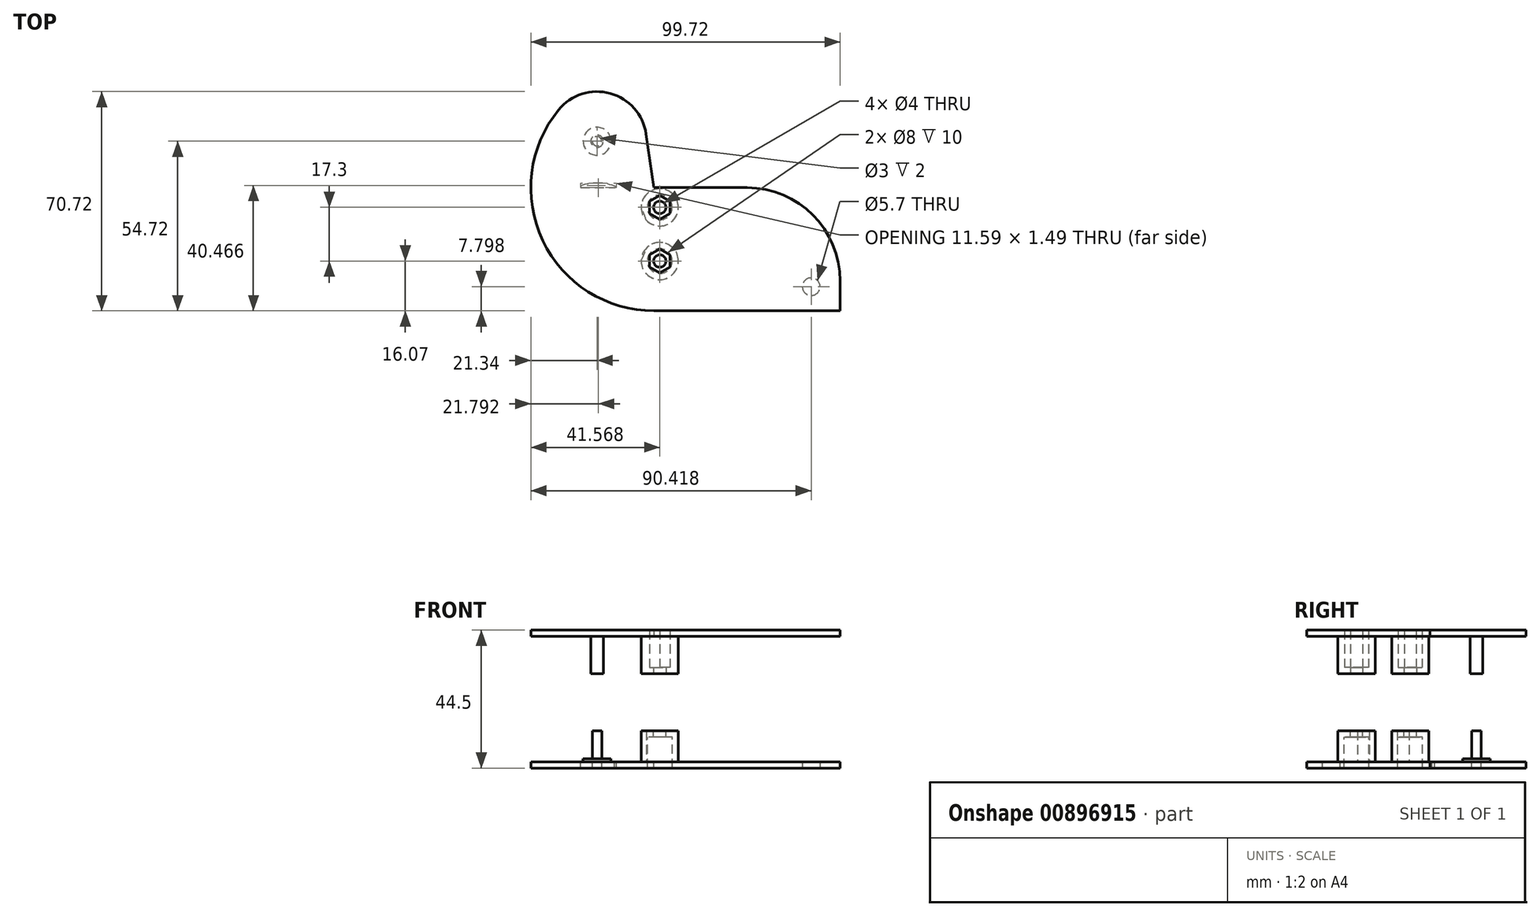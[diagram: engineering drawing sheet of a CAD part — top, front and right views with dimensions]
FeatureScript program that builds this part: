
annotation { "Feature Type Name" : "Feature", "Feature Type Description" : "" }
export const myFeature = defineFeature(function(context is Context, id is Id, definition is map)
    precondition{}
    {
        {
            var Q0;
            Q0=qCreatedBy(makeId("Top.planeOp"),FACE);
            var sketch = newSketch(context, id + "F0", { "sketchPlane" : qUnion([Q0])});
            skPoint(sketch, "E0", {"position": v(20.23, 8.65) * mm});
            skPoint(sketch, "E1", {"position": v(20.23, -8.65) * mm});
            skPoint(sketch, "E2", {"position": v(0, 0) * mm});
            skPoint(sketch, "E3", {"position": v(0, 30) * mm});
            skCircle(sketch, "E4", {"center": v(18.38, 15) * mm, "radius": 23.72 * mm});
            skCircle(sketch, "E5.0", {"center": v(18.38, 15) * mm, "radius": 39.72 * mm});
            skCircle(sketch, "E6", {"center": v(0, 0) * mm, "radius": 16.5 * mm});
            skCircle(sketch, "E7", {"center": v(0, 30) * mm, "radius": 19 * mm});
            skLineSegment(sketch, "E8", {"start": v(-21.34, 15) * mm, "end": v(18.38, 15) * mm});
            skLineSegment(sketch, "E9", {"start": v(18.38, 15) * mm, "end": v(58.1, 15) * mm});
            skLineSegment(sketch, "E10", {"start": v(18.38, -24.72) * mm, "end": v(78.38, -24.72) * mm});
            skLineSegment(sketch, "E11", {"start": v(78.38, -24.72) * mm, "end": v(78.38, 15) * mm});
            skLineSegment(sketch, "E12", {"start": v(78.38, 15) * mm, "end": v(58.1, 15) * mm});
            skCircle(sketch, "E13", {"center": v(20.23, -8.65) * mm, "radius": 4 * mm});
            skCircle(sketch, "E14", {"center": v(20.23, 8.65) * mm, "radius": 4 * mm});
            skCircle(sketch, "E15.0", {"center": v(20.23, -8.65) * mm, "radius": 6 * mm});
            skCircle(sketch, "E16", {"center": v(20.23, 8.65) * mm, "radius": 6 * mm});
            skLineSegment(sketch, "E17", {"start": v(18.38, 15) * mm, "end": v(12.6, 54.3) * mm});
            skCircle(sketch, "E18", {"center": v(0, 30) * mm, "radius": 16 * mm});
            skCircle(sketch, "E19", {"center": v(0, 30) * mm, "radius": 1.5 * mm});
            skCircle(sketch, "E20.0", {"center": v(0, 30) * mm, "radius": 4.5 * mm});
            skSolve(sketch);
        }
        {
            var Q0;
            {var subQ2=sQuery(id+"F0.wireOp",EDGE,"E10");Q0=makeQuery(id+"F0.imprint","IMPRINT",FACE,{"disambiguationData":[TD([[makeQuery(id+"F0.imprint","IMPRINT",EDGE,{"derivedFrom":subQ2}),1.0]])]});}
            var Q1;
            {var subQ4=sQuery(id+"F0.wireOp",EDGE,"E6");var subQ5=sQuery(id+"F0.wireOp",EDGE,"E4");var subQ6=makeQuery(id+"F0.imprint","INTERSECT",VERTEX,{"disambiguationData":[OD(1.0)],"derivedFrom":[subQ5,subQ4]});Q1=makeQuery(id+"F0.imprint","IMPRINT",FACE,{"disambiguationData":[TD([[makeQuery(id+"F0.imprint","IMPRINT",EDGE,{"disambiguationData":[TD([[subQ6,-1.0]])],"derivedFrom":subQ5}),-1.0]])]});}
            var Q2;
            {var subQ0=sQuery(id+"F0.wireOp",EDGE,"E15.0");var subQ1=sQuery(id+"F0.wireOp",EDGE,"E4");var subQ2=makeQuery(id+"F0.imprint","INTERSECT",VERTEX,{"disambiguationData":[OD(0.0)],"derivedFrom":[subQ1,subQ0]});Q2=makeQuery(id+"F0.imprint","IMPRINT",FACE,{"disambiguationData":[TD([[makeQuery(id+"F0.imprint","IMPRINT",EDGE,{"disambiguationData":[TD([[subQ2,-1.0]])],"derivedFrom":subQ1}),-1.0]])]});}
            var Q3;
            {var subQ0=sQuery(id+"F0.wireOp",EDGE,"E15.0");var subQ1=sQuery(id+"F0.wireOp",EDGE,"E4");var subQ2=makeQuery(id+"F0.imprint","INTERSECT",VERTEX,{"disambiguationData":[OD(0.0)],"derivedFrom":[subQ1,subQ0]});Q3=makeQuery(id+"F0.imprint","IMPRINT",FACE,{"disambiguationData":[TD([[makeQuery(id+"F0.imprint","IMPRINT",EDGE,{"disambiguationData":[TD([[subQ2,-1.0]])],"derivedFrom":subQ1}),1.0]])]});}
            var Q4;
            Q4=makeQuery(id+"F0.imprint","IMPRINT",FACE,{"disambiguationData":[TD([[makeQuery(id+"F0.imprint","IMPRINT",EDGE,{"derivedFrom":sQuery(id+"F0.wireOp",EDGE,"E14")}),-1.0]])]});
            var Q5;
            Q5=makeQuery(id+"F0.imprint","IMPRINT",FACE,{"disambiguationData":[TD([[makeQuery(id+"F0.imprint","IMPRINT",EDGE,{"derivedFrom":sQuery(id+"F0.wireOp",EDGE,"E16")}),-1.0]])]});
            var Q6;
            {var subQ0=sQuery(id+"F0.wireOp",EDGE,"E7");var subQ1=sQuery(id+"F0.wireOp",EDGE,"E4");var subQ2=makeQuery(id+"F0.imprint","INTERSECT",VERTEX,{"disambiguationData":[OD(1.0)],"derivedFrom":[subQ1,subQ0]});Q6=makeQuery(id+"F0.imprint","IMPRINT",FACE,{"disambiguationData":[TD([[makeQuery(id+"F0.imprint","IMPRINT",EDGE,{"disambiguationData":[TD([[subQ2,-1.0]])],"derivedFrom":subQ1}),1.0]])]});}
            var Q7;
            {var subQ0=sQuery(id+"F0.wireOp",EDGE,"E8");var subQ1=sQuery(id+"F0.wireOp",EDGE,"E4");var subQ2=makeQuery(id+"F0.imprint","INTERSECT",VERTEX,{"derivedFrom":[subQ1,subQ0]});Q7=makeQuery(id+"F0.imprint","IMPRINT",FACE,{"disambiguationData":[TD([[makeQuery(id+"F0.imprint","IMPRINT",EDGE,{"disambiguationData":[TD([[subQ2,-1.0]])],"derivedFrom":subQ1}),1.0]])]});}
            var Q8;
            {var subQ3=sQuery(id+"F0.wireOp",EDGE,"E4");var subQ6=sQuery(id+"F0.wireOp",EDGE,"E7");var subQ8=makeQuery(id+"F0.imprint","INTERSECT",VERTEX,{"disambiguationData":[OD(1.0)],"derivedFrom":[subQ3,subQ6]});Q8=makeQuery(id+"F0.imprint","IMPRINT",FACE,{"disambiguationData":[TD([[makeQuery(id+"F0.imprint","IMPRINT",EDGE,{"disambiguationData":[TD([[subQ8,-1.0]])],"derivedFrom":subQ3}),-1.0]])]});}
            var Q9;
            {var subQ0=sQuery(id+"F0.wireOp",EDGE,"E8");var subQ1=sQuery(id+"F0.wireOp",EDGE,"E4");var subQ2=makeQuery(id+"F0.imprint","INTERSECT",VERTEX,{"derivedFrom":[subQ1,subQ0]});Q9=makeQuery(id+"F0.imprint","IMPRINT",FACE,{"disambiguationData":[TD([[makeQuery(id+"F0.imprint","IMPRINT",EDGE,{"disambiguationData":[TD([[subQ2,-1.0]])],"derivedFrom":subQ1}),-1.0]])]});}
            var Q10;
            {var subQ0=sQuery(id+"F0.wireOp",EDGE,"E8");var subQ1=sQuery(id+"F0.wireOp",EDGE,"E5.0");var subQ2=makeQuery(id+"F0.imprint","INTERSECT",VERTEX,{"derivedFrom":[subQ1,subQ0]});Q10=makeQuery(id+"F0.imprint","IMPRINT",FACE,{"disambiguationData":[TD([[makeQuery(id+"F0.imprint","IMPRINT",EDGE,{"disambiguationData":[TD([[subQ2,-1.0]])],"derivedFrom":subQ1}),1.0]])]});}
            var Q11;
            {var subQ0=sQuery(id+"F0.wireOp",EDGE,"E8");var subQ1=sQuery(id+"F0.wireOp",EDGE,"E5.0");var subQ2=makeQuery(id+"F0.imprint","INTERSECT",VERTEX,{"derivedFrom":[subQ1,subQ0]});Q11=makeQuery(id+"F0.imprint","IMPRINT",FACE,{"disambiguationData":[TD([[makeQuery(id+"F0.imprint","IMPRINT",EDGE,{"disambiguationData":[TD([[subQ2,1.0]])],"derivedFrom":subQ1}),1.0]])]});}
            var Q12;
            {var subQ0=sQuery(id+"F0.wireOp",EDGE,"E6");var subQ1=sQuery(id+"F0.wireOp",EDGE,"E4");var subQ2=makeQuery(id+"F0.imprint","INTERSECT",VERTEX,{"disambiguationData":[OD(0.0)],"derivedFrom":[subQ1,subQ0]});Q12=makeQuery(id+"F0.imprint","IMPRINT",FACE,{"disambiguationData":[TD([[makeQuery(id+"F0.imprint","IMPRINT",EDGE,{"disambiguationData":[TD([[subQ2,-1.0]])],"derivedFrom":subQ1}),1.0]])]});}
            var Q13;
            {var subQ0=sQuery(id+"F0.wireOp",EDGE,"E6");var subQ1=sQuery(id+"F0.wireOp",EDGE,"E4");var subQ2=makeQuery(id+"F0.imprint","INTERSECT",VERTEX,{"disambiguationData":[OD(0.0)],"derivedFrom":[subQ1,subQ0]});Q13=makeQuery(id+"F0.imprint","IMPRINT",FACE,{"disambiguationData":[TD([[makeQuery(id+"F0.imprint","IMPRINT",EDGE,{"disambiguationData":[TD([[subQ2,-1.0]])],"derivedFrom":subQ1}),-1.0]])]});}
            var Q14;
            {var subQ0=sQuery(id+"F0.wireOp",EDGE,"E17");var subQ1=sQuery(id+"F0.wireOp",EDGE,"E7");var subQ2=makeQuery(id+"F0.imprint","INTERSECT",VERTEX,{"derivedFrom":[subQ1,subQ0]});Q14=makeQuery(id+"F0.imprint","IMPRINT",FACE,{"disambiguationData":[TD([[makeQuery(id+"F0.imprint","IMPRINT",EDGE,{"disambiguationData":[TD([[subQ2,1.0]])],"derivedFrom":subQ1}),-1.0]])]});}
            var Q15;
            {var subQ0=sQuery(id+"F0.wireOp",EDGE,"E18");var subQ1=sQuery(id+"F0.wireOp",EDGE,"E4");var subQ2=makeQuery(id+"F0.imprint","INTERSECT",VERTEX,{"disambiguationData":[OD(0.0)],"derivedFrom":[subQ1,subQ0]});Q15=makeQuery(id+"F0.imprint","IMPRINT",FACE,{"disambiguationData":[TD([[makeQuery(id+"F0.imprint","IMPRINT",EDGE,{"disambiguationData":[TD([[subQ2,-1.0]])],"derivedFrom":subQ1}),-1.0]])]});}
            var Q16;
            {var subQ5=sQuery(id+"F0.wireOp",EDGE,"E4");var subQ7=sQuery(id+"F0.wireOp",EDGE,"E18");var subQ8=makeQuery(id+"F0.imprint","INTERSECT",VERTEX,{"disambiguationData":[OD(1.0)],"derivedFrom":[subQ5,subQ7]});Q16=makeQuery(id+"F0.imprint","IMPRINT",FACE,{"disambiguationData":[TD([[makeQuery(id+"F0.imprint","IMPRINT",EDGE,{"disambiguationData":[TD([[subQ8,-1.0]])],"derivedFrom":subQ5}),-1.0]])]});}
            var Q17;
            {var subQ0=sQuery(id+"F0.wireOp",EDGE,"63ee93db-11cd-4e26-b8ef-de9a7e97acbf.0");var subQ1=sQuery(id+"F0.wireOp",EDGE,"E4");var subQ2=makeQuery(id+"F0.imprint","INTERSECT",VERTEX,{"disambiguationData":[OD(0.0)],"derivedFrom":[subQ1,subQ0]});Q17=makeQuery(id+"F0.imprint","IMPRINT",FACE,{"disambiguationData":[TD([[makeQuery(id+"F0.imprint","IMPRINT",EDGE,{"disambiguationData":[TD([[subQ2,-1.0]])],"derivedFrom":subQ1}),1.0]])]});}
            var Q18;
            {var subQ0=sQuery(id+"F0.wireOp",EDGE,"63ee93db-11cd-4e26-b8ef-de9a7e97acbf.0");var subQ1=sQuery(id+"F0.wireOp",EDGE,"E4");var subQ2=makeQuery(id+"F0.imprint","INTERSECT",VERTEX,{"disambiguationData":[OD(0.0)],"derivedFrom":[subQ1,subQ0]});Q18=makeQuery(id+"F0.imprint","IMPRINT",FACE,{"disambiguationData":[TD([[makeQuery(id+"F0.imprint","IMPRINT",EDGE,{"disambiguationData":[TD([[subQ2,-1.0]])],"derivedFrom":subQ1}),-1.0]])]});}
            var Q19;
            {var subQ0=sQuery(id+"F0.wireOp",EDGE,"E20.0");var subQ1=sQuery(id+"F0.wireOp",EDGE,"E4");var subQ2=makeQuery(id+"F0.imprint","INTERSECT",VERTEX,{"disambiguationData":[OD(0.0)],"derivedFrom":[subQ1,subQ0]});Q19=makeQuery(id+"F0.imprint","IMPRINT",FACE,{"disambiguationData":[TD([[makeQuery(id+"F0.imprint","IMPRINT",EDGE,{"disambiguationData":[TD([[subQ2,-1.0]])],"derivedFrom":subQ1}),-1.0]])]});}
            var Q20;
            {var subQ0=sQuery(id+"F0.wireOp",EDGE,"E20.0");var subQ1=sQuery(id+"F0.wireOp",EDGE,"E4");var subQ2=makeQuery(id+"F0.imprint","INTERSECT",VERTEX,{"disambiguationData":[OD(0.0)],"derivedFrom":[subQ1,subQ0]});Q20=makeQuery(id+"F0.imprint","IMPRINT",FACE,{"disambiguationData":[TD([[makeQuery(id+"F0.imprint","IMPRINT",EDGE,{"disambiguationData":[TD([[subQ2,-1.0]])],"derivedFrom":subQ1}),1.0]])]});}
            var Q21;
            {var subQ3=sQuery(id+"F0.wireOp",EDGE,"E7");var subQ5=sQuery(id+"F0.wireOp",EDGE,"E5.0");var subQ6=makeQuery(id+"F0.imprint","INTERSECT",VERTEX,{"disambiguationData":[OD(1.0)],"derivedFrom":[subQ5,subQ3]});Q21=makeQuery(id+"F0.imprint","IMPRINT",FACE,{"disambiguationData":[TD([[makeQuery(id+"F0.imprint","IMPRINT",EDGE,{"disambiguationData":[TD([[subQ6,1.0]])],"derivedFrom":subQ5}),1.0]])]});}
            var Q22;
            {var subQ0=sQuery(id+"F0.wireOp",EDGE,"E8");var subQ1=sQuery(id+"F0.wireOp",EDGE,"E6");var subQ2=makeQuery(id+"F0.imprint","INTERSECT",VERTEX,{"disambiguationData":[OD(1.0)],"derivedFrom":[subQ1,subQ0]});Q22=makeQuery(id+"F0.imprint","IMPRINT",FACE,{"disambiguationData":[TD([[makeQuery(id+"F0.imprint","IMPRINT",EDGE,{"disambiguationData":[TD([[subQ2,-1.0]])],"derivedFrom":subQ1}),-1.0]])]});}
            var Q23;
            {var subQ0=sQuery(id+"F0.wireOp",EDGE,"E18");var subQ1=sQuery(id+"F0.wireOp",EDGE,"E6");var subQ2=makeQuery(id+"F0.imprint","INTERSECT",VERTEX,{"disambiguationData":[OD(1.0)],"derivedFrom":[subQ1,subQ0]});Q23=makeQuery(id+"F0.imprint","IMPRINT",FACE,{"disambiguationData":[TD([[makeQuery(id+"F0.imprint","IMPRINT",EDGE,{"disambiguationData":[TD([[subQ2,-1.0]])],"derivedFrom":subQ1}),1.0]])]});}
            var Q24;
            {var subQ5=sQuery(id+"F0.wireOp",EDGE,"E8");var subQ7=sQuery(id+"F0.wireOp",EDGE,"E6");var subQ9=makeQuery(id+"F0.imprint","INTERSECT",VERTEX,{"disambiguationData":[OD(0.0)],"derivedFrom":[subQ7,subQ5]});Q24=makeQuery(id+"F0.imprint","IMPRINT",FACE,{"disambiguationData":[TD([[makeQuery(id+"F0.imprint","IMPRINT",EDGE,{"disambiguationData":[TD([[subQ9,-1.0]])],"derivedFrom":subQ7}),-1.0]])]});}
            var Q25;
            {var subQ0=sQuery(id+"F0.wireOp",EDGE,"E8");var subQ1=sQuery(id+"F0.wireOp",EDGE,"E6");var subQ2=makeQuery(id+"F0.imprint","INTERSECT",VERTEX,{"disambiguationData":[OD(0.0)],"derivedFrom":[subQ1,subQ0]});Q25=makeQuery(id+"F0.imprint","IMPRINT",FACE,{"disambiguationData":[TD([[makeQuery(id+"F0.imprint","IMPRINT",EDGE,{"disambiguationData":[TD([[subQ2,1.0]])],"derivedFrom":subQ1}),-1.0]])]});}
            var Q26;
            {var subQ0=sQuery(id+"F0.wireOp",EDGE,"E18");var subQ1=sQuery(id+"F0.wireOp",EDGE,"E4");var subQ2=makeQuery(id+"F0.imprint","INTERSECT",VERTEX,{"disambiguationData":[OD(0.0)],"derivedFrom":[subQ1,subQ0]});Q26=makeQuery(id+"F0.imprint","IMPRINT",FACE,{"disambiguationData":[TD([[makeQuery(id+"F0.imprint","IMPRINT",EDGE,{"disambiguationData":[TD([[subQ2,-1.0]])],"derivedFrom":subQ1}),1.0]])]});}
            var Q27;
            {var subQ0=sQuery(id+"F0.wireOp",EDGE,"E8");var subQ1=sQuery(id+"F0.wireOp",EDGE,"E6");var subQ2=makeQuery(id+"F0.imprint","INTERSECT",VERTEX,{"disambiguationData":[OD(0.0)],"derivedFrom":[subQ1,subQ0]});Q27=makeQuery(id+"F0.imprint","IMPRINT",FACE,{"disambiguationData":[TD([[makeQuery(id+"F0.imprint","IMPRINT",EDGE,{"disambiguationData":[TD([[subQ2,-1.0]])],"derivedFrom":subQ1}),1.0]])]});}
            var Q28;
            {var subQ1=sQuery(id+"F0.wireOp",EDGE,"E4");var subQ5=sQuery(id+"F0.wireOp",EDGE,"E18");var subQ6=makeQuery(id+"F0.imprint","INTERSECT",VERTEX,{"disambiguationData":[OD(1.0)],"derivedFrom":[subQ1,subQ5]});Q28=makeQuery(id+"F0.imprint","IMPRINT",FACE,{"disambiguationData":[TD([[makeQuery(id+"F0.imprint","IMPRINT",EDGE,{"disambiguationData":[TD([[subQ6,-1.0]])],"derivedFrom":subQ1}),1.0]])]});}
            var Q29;
            {var subQ0=sQuery(id+"F0.wireOp",EDGE,"E16");var subQ1=sQuery(id+"F0.wireOp",EDGE,"E6");var subQ2=makeQuery(id+"F0.imprint","INTERSECT",VERTEX,{"disambiguationData":[OD(0.0)],"derivedFrom":[subQ1,subQ0]});Q29=makeQuery(id+"F0.imprint","IMPRINT",FACE,{"disambiguationData":[TD([[makeQuery(id+"F0.imprint","IMPRINT",EDGE,{"disambiguationData":[TD([[subQ2,1.0]])],"derivedFrom":subQ1}),1.0]])]});}
            var Q30;
            {var subQ0=sQuery(id+"F0.wireOp",EDGE,"E15.0");var subQ1=sQuery(id+"F0.wireOp",EDGE,"E6");var subQ2=makeQuery(id+"F0.imprint","INTERSECT",VERTEX,{"disambiguationData":[OD(0.0)],"derivedFrom":[subQ1,subQ0]});Q30=makeQuery(id+"F0.imprint","IMPRINT",FACE,{"disambiguationData":[TD([[makeQuery(id+"F0.imprint","IMPRINT",EDGE,{"disambiguationData":[TD([[subQ2,-1.0]])],"derivedFrom":subQ1}),1.0]])]});}
            var Q31;
            {var subQ9=sQuery(id+"F0.wireOp",EDGE,"E9");var subQ11=sQuery(id+"F0.wireOp",EDGE,"E4");var subQ12=makeQuery(id+"F0.imprint","INTERSECT",VERTEX,{"derivedFrom":[subQ11,subQ9]});Q31=makeQuery(id+"F0.imprint","IMPRINT",FACE,{"disambiguationData":[TD([[makeQuery(id+"F0.imprint","IMPRINT",EDGE,{"disambiguationData":[TD([[subQ12,1.0]])],"derivedFrom":subQ11}),1.0]])]});}
            extrude(context, id + "F1", {"entities" : qUnion([Q0, Q1, Q2, Q3, Q4, Q5, Q6, Q7, Q8, Q9, Q10, Q11, Q12, Q13, Q14, Q15, Q16, Q17, Q18, Q19, Q20, Q21, Q22, Q23, Q24, Q25, Q26, Q27, Q28, Q29, Q30, Q31]), "oppositeDirection" : true, "depth" : 2 * mm, "offsetDistance" : 25 * mm});
        }
        {
            var Q0;
            {var subQ0=sQuery(id+"F0.wireOp",EDGE,"E20.0");var subQ1=sQuery(id+"F0.wireOp",EDGE,"E4");var subQ2=makeQuery(id+"F0.imprint","INTERSECT",VERTEX,{"disambiguationData":[OD(0.0)],"derivedFrom":[subQ1,subQ0]});Q0=makeQuery(id+"F0.imprint","IMPRINT",FACE,{"disambiguationData":[TD([[makeQuery(id+"F0.imprint","IMPRINT",EDGE,{"disambiguationData":[TD([[subQ2,-1.0]])],"derivedFrom":subQ1}),1.0]])]});}
            var Q1;
            {var subQ0=sQuery(id+"F0.wireOp",EDGE,"E20.0");var subQ1=sQuery(id+"F0.wireOp",EDGE,"E4");var subQ2=makeQuery(id+"F0.imprint","INTERSECT",VERTEX,{"disambiguationData":[OD(0.0)],"derivedFrom":[subQ1,subQ0]});Q1=makeQuery(id+"F0.imprint","IMPRINT",FACE,{"disambiguationData":[TD([[makeQuery(id+"F0.imprint","IMPRINT",EDGE,{"disambiguationData":[TD([[subQ2,-1.0]])],"derivedFrom":subQ1}),-1.0]])]});}
            extrude(context, id + "F2", {"entities" : qUnion([Q0, Q1]), "operationType" : NewBodyOperationType.ADD, "depth" : 1 * mm, "offsetDistance" : 25 * mm});
        }
        {
            var Q0;
            {var subQ0=sQuery(id+"F0.wireOp",EDGE,"E19");var subQ1=sQuery(id+"F0.wireOp",EDGE,"E4");var subQ2=makeQuery(id+"F0.imprint","INTERSECT",VERTEX,{"disambiguationData":[OD(0.0)],"derivedFrom":[subQ1,subQ0]});Q0=makeQuery(id+"F0.imprint","IMPRINT",FACE,{"disambiguationData":[TD([[makeQuery(id+"F0.imprint","IMPRINT",EDGE,{"disambiguationData":[TD([[subQ2,-1.0]])],"derivedFrom":subQ1}),1.0]])]});}
            var Q1;
            {var subQ0=sQuery(id+"F0.wireOp",EDGE,"E19");var subQ1=sQuery(id+"F0.wireOp",EDGE,"E4");var subQ2=makeQuery(id+"F0.imprint","INTERSECT",VERTEX,{"disambiguationData":[OD(0.0)],"derivedFrom":[subQ1,subQ0]});Q1=makeQuery(id+"F0.imprint","IMPRINT",FACE,{"disambiguationData":[TD([[makeQuery(id+"F0.imprint","IMPRINT",EDGE,{"disambiguationData":[TD([[subQ2,-1.0]])],"derivedFrom":subQ1}),-1.0]])]});}
            extrude(context, id + "F3", {"entities" : qUnion([Q0, Q1]), "operationType" : NewBodyOperationType.ADD, "depth" : 10 * mm, "offsetDistance" : 25 * mm});
        }
        {
            var Q0;
            {var subQ0=sQuery(id+"F0.wireOp",EDGE,"E15.0");var subQ1=sQuery(id+"F0.wireOp",EDGE,"E4");var subQ2=makeQuery(id+"F0.imprint","INTERSECT",VERTEX,{"disambiguationData":[OD(0.0)],"derivedFrom":[subQ1,subQ0]});Q0=makeQuery(id+"F0.imprint","IMPRINT",FACE,{"disambiguationData":[TD([[makeQuery(id+"F0.imprint","IMPRINT",EDGE,{"disambiguationData":[TD([[subQ2,-1.0]])],"derivedFrom":subQ1}),-1.0]])]});}
            var Q1;
            Q1=makeQuery(id+"F0.imprint","IMPRINT",FACE,{"disambiguationData":[TD([[makeQuery(id+"F0.imprint","IMPRINT",EDGE,{"derivedFrom":sQuery(id+"F0.wireOp",EDGE,"E14")}),-1.0]])]});
            var Q2;
            {var subQ0=sQuery(id+"F0.wireOp",EDGE,"E15.0");var subQ1=sQuery(id+"F0.wireOp",EDGE,"E4");var subQ2=makeQuery(id+"F0.imprint","INTERSECT",VERTEX,{"disambiguationData":[OD(0.0)],"derivedFrom":[subQ1,subQ0]});Q2=makeQuery(id+"F0.imprint","IMPRINT",FACE,{"disambiguationData":[TD([[makeQuery(id+"F0.imprint","IMPRINT",EDGE,{"disambiguationData":[TD([[subQ2,-1.0]])],"derivedFrom":subQ1}),1.0]])]});}
            extrude(context, id + "F4", {"entities" : qUnion([Q0, Q1, Q2]), "operationType" : NewBodyOperationType.ADD, "depth" : 10 * mm, "offsetDistance" : 25 * mm});
        }
        {
            var Q0;
            Q0=makeQuery(id+"F4.opExtrude","CAP_FACE",FACE,{"disambiguationData":[OSD([sQuery(id+"F0.wireOp",EDGE,"E13"),sQuery(id+"F0.wireOp",EDGE,"E15.0")])],"isStart":false});
            var sketch = newSketch(context, id + "F5", { "sketchPlane" : qUnion([Q0])});
            skCircle(sketch, "E21", {"center": v(20.23, -8.65) * mm, "radius": 4 * mm});
            skCircle(sketch, "E22", {"center": v(20.23, -8.65) * mm, "radius": 2 * mm});
            skCircle(sketch, "E23", {"center": v(20.23, 8.65) * mm, "radius": 4 * mm});
            skCircle(sketch, "E24", {"center": v(20.23, 8.65) * mm, "radius": 2 * mm});
            skSolve(sketch);
        }
        {
            var Q0;
            Q0=makeQuery(id+"F5.imprint","IMPRINT",FACE,{"disambiguationData":[TD([[makeQuery(id+"F5.imprint","IMPRINT",EDGE,{"derivedFrom":sQuery(id+"F5.wireOp",EDGE,"E23")}),1.0]])]});
            var Q1;
            Q1=makeQuery(id+"F5.imprint","IMPRINT",FACE,{"disambiguationData":[TD([[makeQuery(id+"F5.imprint","IMPRINT",EDGE,{"derivedFrom":sQuery(id+"F5.wireOp",EDGE,"E21")}),1.0]])]});
            extrude(context, id + "F6", {"entities" : qUnion([Q0, Q1]), "operationType" : NewBodyOperationType.ADD, "oppositeDirection" : true, "depth" : 2 * mm, "offsetDistance" : 25 * mm});
        }
        {
            var Q0;
            Q0=qCreatedBy(makeId("Top.planeOp"),FACE);
            cPlane(context, id + "F7", {"entities" : qUnion([Q0]), "cplaneType" : CPlaneType.OFFSET, "offset" : 40.5 * mm, "width" : 150 * mm, "height" : 150 * mm});
        }
        {
            var Q0;
            Q0=qCreatedBy(id+"F7.planeOp",FACE);
            var sketch = newSketch(context, id + "F8", { "sketchPlane" : qUnion([Q0])});
            skPoint(sketch, "E25", {"position": v(20.23, 8.65) * mm});
            skPoint(sketch, "E26", {"position": v(20.23, -8.65) * mm});
            skPoint(sketch, "E27", {"position": v(0, 0) * mm});
            skPoint(sketch, "E28", {"position": v(0, 30) * mm});
            skCircle(sketch, "E29", {"center": v(18.38, 15) * mm, "radius": 23.72 * mm});
            skCircle(sketch, "E30.0", {"center": v(18.38, 15) * mm, "radius": 39.72 * mm});
            skCircle(sketch, "E31", {"center": v(0, 0) * mm, "radius": 16.5 * mm});
            skCircle(sketch, "E32", {"center": v(0, 30) * mm, "radius": 19 * mm});
            skLineSegment(sketch, "E33", {"start": v(-21.34, 15) * mm, "end": v(18.38, 15) * mm});
            skLineSegment(sketch, "E34", {"start": v(18.38, 15) * mm, "end": v(58.1, 15) * mm});
            skLineSegment(sketch, "E35", {"start": v(18.38, -24.72) * mm, "end": v(78.38, -24.72) * mm});
            skLineSegment(sketch, "E36", {"start": v(78.38, -24.72) * mm, "end": v(78.38, 15) * mm});
            skLineSegment(sketch, "E37", {"start": v(78.38, 15) * mm, "end": v(58.1, 15) * mm});
            skCircle(sketch, "E38.0", {"center": v(20.23, -8.65) * mm, "radius": 6 * mm});
            skCircle(sketch, "E39", {"center": v(20.23, 8.65) * mm, "radius": 6 * mm});
            skLineSegment(sketch, "E40", {"start": v(18.38, 15) * mm, "end": v(12.6, 54.3) * mm});
            skCircle(sketch, "E41", {"center": v(0, 30) * mm, "radius": 16 * mm});
            skCircle(sketch, "E42", {"center": v(0, 30) * mm, "radius": 2 * mm});
            skCircle(sketch, "E43.0", {"center": v(0, 30) * mm, "radius": 4 * mm});
            skCircle(sketch, "E44.cCircle", {"center": v(20.23, 8.65) * mm, "radius": 3.35 * mm, "construction": true});
            skLineSegment(sketch, "E44.0", {"start": v(23.58, 10.58) * mm, "end": v(23.58, 6.72) * mm});
            skLineSegment(sketch, "E44.1", {"start": v(23.58, 6.72) * mm, "end": v(20.23, 4.78) * mm});
            skLineSegment(sketch, "E44.2", {"start": v(20.23, 4.78) * mm, "end": v(16.88, 6.72) * mm});
            skLineSegment(sketch, "E44.3", {"start": v(16.88, 6.72) * mm, "end": v(16.88, 10.58) * mm});
            skLineSegment(sketch, "E44.4", {"start": v(16.88, 10.58) * mm, "end": v(20.23, 12.52) * mm});
            skLineSegment(sketch, "E44.5", {"start": v(20.23, 12.52) * mm, "end": v(23.58, 10.58) * mm});
            skPoint(sketch, "E44.0.midPoint", {"position": v(23.58, 8.65) * mm});
            skCircle(sketch, "E45.cCircle", {"center": v(20.23, -8.65) * mm, "radius": 3.35 * mm, "construction": true});
            skLineSegment(sketch, "E45.0", {"start": v(16.88, -6.72) * mm, "end": v(20.23, -4.78) * mm});
            skLineSegment(sketch, "E45.1", {"start": v(20.23, -4.78) * mm, "end": v(23.58, -6.72) * mm});
            skLineSegment(sketch, "E45.2", {"start": v(23.58, -6.72) * mm, "end": v(23.58, -10.58) * mm});
            skLineSegment(sketch, "E45.3", {"start": v(23.58, -10.58) * mm, "end": v(20.23, -12.52) * mm});
            skLineSegment(sketch, "E45.4", {"start": v(20.23, -12.52) * mm, "end": v(16.88, -10.58) * mm});
            skLineSegment(sketch, "E45.5", {"start": v(16.88, -10.58) * mm, "end": v(16.88, -6.72) * mm});
            skPoint(sketch, "E45.0.midPoint", {"position": v(18.55, -5.75) * mm});
            skSolve(sketch);
        }
        {
            var Q0;
            {var subQ2=sQuery(id+"F8.wireOp",EDGE,"E35");Q0=makeQuery(id+"F8.imprint","IMPRINT",FACE,{"disambiguationData":[TD([[makeQuery(id+"F8.imprint","IMPRINT",EDGE,{"derivedFrom":subQ2}),1.0]])]});}
            var Q1;
            {var subQ4=sQuery(id+"F8.wireOp",EDGE,"E31");var subQ6=sQuery(id+"F8.wireOp",EDGE,"E29");var subQ7=makeQuery(id+"F8.imprint","INTERSECT",VERTEX,{"disambiguationData":[OD(1.0)],"derivedFrom":[subQ6,subQ4]});Q1=makeQuery(id+"F8.imprint","IMPRINT",FACE,{"disambiguationData":[TD([[makeQuery(id+"F8.imprint","IMPRINT",EDGE,{"disambiguationData":[TD([[subQ7,-1.0]])],"derivedFrom":subQ6}),-1.0]])]});}
            var Q2;
            {var subQ5=sQuery(id+"F8.wireOp",EDGE,"E45.0");Q2=makeQuery(id+"F8.imprint","IMPRINT",FACE,{"disambiguationData":[TD([[makeQuery(id+"F8.imprint","IMPRINT",EDGE,{"derivedFrom":subQ5}),1.0]])]});}
            var Q3;
            {var subQ4=sQuery(id+"F8.wireOp",EDGE,"E45.3");Q3=makeQuery(id+"F8.imprint","IMPRINT",FACE,{"disambiguationData":[TD([[makeQuery(id+"F8.imprint","IMPRINT",EDGE,{"derivedFrom":subQ4}),1.0]])]});}
            var Q4;
            {var subQ9=sQuery(id+"F8.wireOp",EDGE,"E34");var subQ11=sQuery(id+"F8.wireOp",EDGE,"E29");var subQ12=makeQuery(id+"F8.imprint","INTERSECT",VERTEX,{"derivedFrom":[subQ11,subQ9]});Q4=makeQuery(id+"F8.imprint","IMPRINT",FACE,{"disambiguationData":[TD([[makeQuery(id+"F8.imprint","IMPRINT",EDGE,{"disambiguationData":[TD([[subQ12,1.0]])],"derivedFrom":subQ11}),1.0]])]});}
            var Q5;
            Q5=makeQuery(id+"F8.imprint","IMPRINT",FACE,{"disambiguationData":[TD([[makeQuery(id+"F8.imprint","IMPRINT",EDGE,{"derivedFrom":sQuery(id+"F8.wireOp",EDGE,"E44.0")}),1.0]])]});
            var Q6;
            {var subQ5=sQuery(id+"F8.wireOp",EDGE,"E29");var subQ9=sQuery(id+"F8.wireOp",EDGE,"E32");var subQ11=makeQuery(id+"F8.imprint","INTERSECT",VERTEX,{"disambiguationData":[OD(1.0)],"derivedFrom":[subQ5,subQ9]});Q6=makeQuery(id+"F8.imprint","IMPRINT",FACE,{"disambiguationData":[TD([[makeQuery(id+"F8.imprint","IMPRINT",EDGE,{"disambiguationData":[TD([[subQ11,-1.0]])],"derivedFrom":subQ5}),1.0]])]});}
            var Q7;
            {var subQ3=sQuery(id+"F8.wireOp",EDGE,"E32");var subQ6=sQuery(id+"F8.wireOp",EDGE,"E29");var subQ7=makeQuery(id+"F8.imprint","INTERSECT",VERTEX,{"disambiguationData":[OD(1.0)],"derivedFrom":[subQ6,subQ3]});Q7=makeQuery(id+"F8.imprint","IMPRINT",FACE,{"disambiguationData":[TD([[makeQuery(id+"F8.imprint","IMPRINT",EDGE,{"disambiguationData":[TD([[subQ7,-1.0]])],"derivedFrom":subQ6}),-1.0]])]});}
            var Q8;
            {var subQ0=sQuery(id+"F8.wireOp",EDGE,"E33");var subQ1=sQuery(id+"F8.wireOp",EDGE,"E30.0");var subQ2=makeQuery(id+"F8.imprint","INTERSECT",VERTEX,{"derivedFrom":[subQ1,subQ0]});Q8=makeQuery(id+"F8.imprint","IMPRINT",FACE,{"disambiguationData":[TD([[makeQuery(id+"F8.imprint","IMPRINT",EDGE,{"disambiguationData":[TD([[subQ2,-1.0]])],"derivedFrom":subQ1}),1.0]])]});}
            var Q9;
            {var subQ0=sQuery(id+"F8.wireOp",EDGE,"E41");var subQ1=sQuery(id+"F8.wireOp",EDGE,"E29");var subQ2=makeQuery(id+"F8.imprint","INTERSECT",VERTEX,{"disambiguationData":[OD(0.0)],"derivedFrom":[subQ1,subQ0]});Q9=makeQuery(id+"F8.imprint","IMPRINT",FACE,{"disambiguationData":[TD([[makeQuery(id+"F8.imprint","IMPRINT",EDGE,{"disambiguationData":[TD([[subQ2,-1.0]])],"derivedFrom":subQ1}),-1.0]])]});}
            var Q10;
            {var subQ3=sQuery(id+"F8.wireOp",EDGE,"E32");var subQ5=sQuery(id+"F8.wireOp",EDGE,"E30.0");var subQ6=makeQuery(id+"F8.imprint","INTERSECT",VERTEX,{"disambiguationData":[OD(1.0)],"derivedFrom":[subQ5,subQ3]});Q10=makeQuery(id+"F8.imprint","IMPRINT",FACE,{"disambiguationData":[TD([[makeQuery(id+"F8.imprint","IMPRINT",EDGE,{"disambiguationData":[TD([[subQ6,1.0]])],"derivedFrom":subQ5}),1.0]])]});}
            var Q11;
            {var subQ0=sQuery(id+"F8.wireOp",EDGE,"E33");var subQ1=sQuery(id+"F8.wireOp",EDGE,"E30.0");var subQ2=makeQuery(id+"F8.imprint","INTERSECT",VERTEX,{"derivedFrom":[subQ1,subQ0]});Q11=makeQuery(id+"F8.imprint","IMPRINT",FACE,{"disambiguationData":[TD([[makeQuery(id+"F8.imprint","IMPRINT",EDGE,{"disambiguationData":[TD([[subQ2,1.0]])],"derivedFrom":subQ1}),1.0]])]});}
            var Q12;
            {var subQ3=sQuery(id+"F8.wireOp",EDGE,"E41");var subQ7=sQuery(id+"F8.wireOp",EDGE,"E29");var subQ9=makeQuery(id+"F8.imprint","INTERSECT",VERTEX,{"disambiguationData":[OD(1.0)],"derivedFrom":[subQ7,subQ3]});Q12=makeQuery(id+"F8.imprint","IMPRINT",FACE,{"disambiguationData":[TD([[makeQuery(id+"F8.imprint","IMPRINT",EDGE,{"disambiguationData":[TD([[subQ9,-1.0]])],"derivedFrom":subQ7}),-1.0]])]});}
            var Q13;
            {var subQ0=sQuery(id+"F8.wireOp",EDGE,"E33");var subQ1=sQuery(id+"F8.wireOp",EDGE,"E31");var subQ2=makeQuery(id+"F8.imprint","INTERSECT",VERTEX,{"disambiguationData":[OD(1.0)],"derivedFrom":[subQ1,subQ0]});Q13=makeQuery(id+"F8.imprint","IMPRINT",FACE,{"disambiguationData":[TD([[makeQuery(id+"F8.imprint","IMPRINT",EDGE,{"disambiguationData":[TD([[subQ2,-1.0]])],"derivedFrom":subQ1}),-1.0]])]});}
            var Q14;
            {var subQ0=sQuery(id+"F8.wireOp",EDGE,"E31");var subQ1=sQuery(id+"F8.wireOp",EDGE,"E29");var subQ2=makeQuery(id+"F8.imprint","INTERSECT",VERTEX,{"disambiguationData":[OD(0.0)],"derivedFrom":[subQ1,subQ0]});Q14=makeQuery(id+"F8.imprint","IMPRINT",FACE,{"disambiguationData":[TD([[makeQuery(id+"F8.imprint","IMPRINT",EDGE,{"disambiguationData":[TD([[subQ2,-1.0]])],"derivedFrom":subQ1}),-1.0]])]});}
            var Q15;
            {var subQ0=sQuery(id+"F8.wireOp",EDGE,"E41");var subQ1=sQuery(id+"F8.wireOp",EDGE,"E29");var subQ2=makeQuery(id+"F8.imprint","INTERSECT",VERTEX,{"disambiguationData":[OD(0.0)],"derivedFrom":[subQ1,subQ0]});Q15=makeQuery(id+"F8.imprint","IMPRINT",FACE,{"disambiguationData":[TD([[makeQuery(id+"F8.imprint","IMPRINT",EDGE,{"disambiguationData":[TD([[subQ2,-1.0]])],"derivedFrom":subQ1}),1.0]])]});}
            var Q16;
            {var subQ1=sQuery(id+"F8.wireOp",EDGE,"E29");var subQ5=sQuery(id+"F8.wireOp",EDGE,"E41");var subQ6=makeQuery(id+"F8.imprint","INTERSECT",VERTEX,{"disambiguationData":[OD(1.0)],"derivedFrom":[subQ1,subQ5]});Q16=makeQuery(id+"F8.imprint","IMPRINT",FACE,{"disambiguationData":[TD([[makeQuery(id+"F8.imprint","IMPRINT",EDGE,{"disambiguationData":[TD([[subQ6,-1.0]])],"derivedFrom":subQ1}),1.0]])]});}
            var Q17;
            {var subQ0=sQuery(id+"F8.wireOp",EDGE,"E31");var subQ1=sQuery(id+"F8.wireOp",EDGE,"E29");var subQ2=makeQuery(id+"F8.imprint","INTERSECT",VERTEX,{"disambiguationData":[OD(0.0)],"derivedFrom":[subQ1,subQ0]});Q17=makeQuery(id+"F8.imprint","IMPRINT",FACE,{"disambiguationData":[TD([[makeQuery(id+"F8.imprint","IMPRINT",EDGE,{"disambiguationData":[TD([[subQ2,-1.0]])],"derivedFrom":subQ1}),1.0]])]});}
            var Q18;
            {var subQ0=sQuery(id+"F8.wireOp",EDGE,"E41");var subQ1=sQuery(id+"F8.wireOp",EDGE,"E31");var subQ2=makeQuery(id+"F8.imprint","INTERSECT",VERTEX,{"disambiguationData":[OD(1.0)],"derivedFrom":[subQ1,subQ0]});Q18=makeQuery(id+"F8.imprint","IMPRINT",FACE,{"disambiguationData":[TD([[makeQuery(id+"F8.imprint","IMPRINT",EDGE,{"disambiguationData":[TD([[subQ2,-1.0]])],"derivedFrom":subQ1}),1.0]])]});}
            var Q19;
            {var subQ0=sQuery(id+"F8.wireOp",EDGE,"E33");var subQ1=sQuery(id+"F8.wireOp",EDGE,"E29");var subQ2=makeQuery(id+"F8.imprint","INTERSECT",VERTEX,{"derivedFrom":[subQ1,subQ0]});Q19=makeQuery(id+"F8.imprint","IMPRINT",FACE,{"disambiguationData":[TD([[makeQuery(id+"F8.imprint","IMPRINT",EDGE,{"disambiguationData":[TD([[subQ2,-1.0]])],"derivedFrom":subQ1}),1.0]])]});}
            var Q20;
            {var subQ0=sQuery(id+"F8.wireOp",EDGE,"E33");var subQ1=sQuery(id+"F8.wireOp",EDGE,"E29");var subQ2=makeQuery(id+"F8.imprint","INTERSECT",VERTEX,{"derivedFrom":[subQ1,subQ0]});Q20=makeQuery(id+"F8.imprint","IMPRINT",FACE,{"disambiguationData":[TD([[makeQuery(id+"F8.imprint","IMPRINT",EDGE,{"disambiguationData":[TD([[subQ2,-1.0]])],"derivedFrom":subQ1}),-1.0]])]});}
            var Q21;
            {var subQ0=sQuery(id+"F8.wireOp",EDGE,"E43.0");var subQ1=sQuery(id+"F8.wireOp",EDGE,"E29");var subQ2=makeQuery(id+"F8.imprint","INTERSECT",VERTEX,{"disambiguationData":[OD(0.0)],"derivedFrom":[subQ1,subQ0]});Q21=makeQuery(id+"F8.imprint","IMPRINT",FACE,{"disambiguationData":[TD([[makeQuery(id+"F8.imprint","IMPRINT",EDGE,{"disambiguationData":[TD([[subQ2,-1.0]])],"derivedFrom":subQ1}),-1.0]])]});}
            var Q22;
            {var subQ0=sQuery(id+"F8.wireOp",EDGE,"E43.0");var subQ1=sQuery(id+"F8.wireOp",EDGE,"E29");var subQ2=makeQuery(id+"F8.imprint","INTERSECT",VERTEX,{"disambiguationData":[OD(0.0)],"derivedFrom":[subQ1,subQ0]});Q22=makeQuery(id+"F8.imprint","IMPRINT",FACE,{"disambiguationData":[TD([[makeQuery(id+"F8.imprint","IMPRINT",EDGE,{"disambiguationData":[TD([[subQ2,-1.0]])],"derivedFrom":subQ1}),1.0]])]});}
            var Q23;
            {var subQ0=sQuery(id+"F8.wireOp",EDGE,"E42");var subQ1=sQuery(id+"F8.wireOp",EDGE,"E29");var subQ2=makeQuery(id+"F8.imprint","INTERSECT",VERTEX,{"disambiguationData":[OD(0.0)],"derivedFrom":[subQ1,subQ0]});Q23=makeQuery(id+"F8.imprint","IMPRINT",FACE,{"disambiguationData":[TD([[makeQuery(id+"F8.imprint","IMPRINT",EDGE,{"disambiguationData":[TD([[subQ2,-1.0]])],"derivedFrom":subQ1}),-1.0]])]});}
            var Q24;
            {var subQ0=sQuery(id+"F8.wireOp",EDGE,"E42");var subQ1=sQuery(id+"F8.wireOp",EDGE,"E29");var subQ2=makeQuery(id+"F8.imprint","INTERSECT",VERTEX,{"disambiguationData":[OD(0.0)],"derivedFrom":[subQ1,subQ0]});Q24=makeQuery(id+"F8.imprint","IMPRINT",FACE,{"disambiguationData":[TD([[makeQuery(id+"F8.imprint","IMPRINT",EDGE,{"disambiguationData":[TD([[subQ2,-1.0]])],"derivedFrom":subQ1}),1.0]])]});}
            var Q25;
            {var subQ5=sQuery(id+"F8.wireOp",EDGE,"E33");var subQ7=sQuery(id+"F8.wireOp",EDGE,"E31");var subQ9=makeQuery(id+"F8.imprint","INTERSECT",VERTEX,{"disambiguationData":[OD(0.0)],"derivedFrom":[subQ7,subQ5]});Q25=makeQuery(id+"F8.imprint","IMPRINT",FACE,{"disambiguationData":[TD([[makeQuery(id+"F8.imprint","IMPRINT",EDGE,{"disambiguationData":[TD([[subQ9,-1.0]])],"derivedFrom":subQ7}),-1.0]])]});}
            var Q26;
            {var subQ0=sQuery(id+"F8.wireOp",EDGE,"E33");var subQ1=sQuery(id+"F8.wireOp",EDGE,"E32");var subQ2=makeQuery(id+"F8.imprint","INTERSECT",VERTEX,{"disambiguationData":[OD(1.0)],"derivedFrom":[subQ1,subQ0]});Q26=makeQuery(id+"F8.imprint","IMPRINT",FACE,{"disambiguationData":[TD([[makeQuery(id+"F8.imprint","IMPRINT",EDGE,{"disambiguationData":[TD([[subQ2,-1.0]])],"derivedFrom":subQ1}),-1.0]])]});}
            var Q27;
            {var subQ0=sQuery(id+"F8.wireOp",EDGE,"E33");var subQ1=sQuery(id+"F8.wireOp",EDGE,"E31");var subQ2=makeQuery(id+"F8.imprint","INTERSECT",VERTEX,{"disambiguationData":[OD(0.0)],"derivedFrom":[subQ1,subQ0]});Q27=makeQuery(id+"F8.imprint","IMPRINT",FACE,{"disambiguationData":[TD([[makeQuery(id+"F8.imprint","IMPRINT",EDGE,{"disambiguationData":[TD([[subQ2,-1.0]])],"derivedFrom":subQ1}),1.0]])]});}
            var Q28;
            {var subQ0=sQuery(id+"F8.wireOp",EDGE,"E32");var subQ1=sQuery(id+"F8.wireOp",EDGE,"E31");var subQ2=makeQuery(id+"F8.imprint","INTERSECT",VERTEX,{"disambiguationData":[OD(0.0)],"derivedFrom":[subQ1,subQ0]});Q28=makeQuery(id+"F8.imprint","IMPRINT",FACE,{"disambiguationData":[TD([[makeQuery(id+"F8.imprint","IMPRINT",EDGE,{"disambiguationData":[TD([[subQ2,-1.0]])],"derivedFrom":subQ1}),-1.0]])]});}
            var Q29;
            {var subQ0=sQuery(id+"F8.wireOp",EDGE,"E39");var subQ1=sQuery(id+"F8.wireOp",EDGE,"E31");var subQ2=makeQuery(id+"F8.imprint","INTERSECT",VERTEX,{"disambiguationData":[OD(0.0)],"derivedFrom":[subQ1,subQ0]});Q29=makeQuery(id+"F8.imprint","IMPRINT",FACE,{"disambiguationData":[TD([[makeQuery(id+"F8.imprint","IMPRINT",EDGE,{"disambiguationData":[TD([[subQ2,1.0]])],"derivedFrom":subQ1}),1.0]])]});}
            var Q30;
            {var subQ0=sQuery(id+"F8.wireOp",EDGE,"E38.0");var subQ1=sQuery(id+"F8.wireOp",EDGE,"E31");var subQ2=makeQuery(id+"F8.imprint","INTERSECT",VERTEX,{"disambiguationData":[OD(0.0)],"derivedFrom":[subQ1,subQ0]});Q30=makeQuery(id+"F8.imprint","IMPRINT",FACE,{"disambiguationData":[TD([[makeQuery(id+"F8.imprint","IMPRINT",EDGE,{"disambiguationData":[TD([[subQ2,-1.0]])],"derivedFrom":subQ1}),1.0]])]});}
            var Q31;
            {var subQ0=sQuery(id+"F8.wireOp",EDGE,"E31");var subQ1=sQuery(id+"F8.wireOp",EDGE,"E29");var subQ2=makeQuery(id+"F8.imprint","INTERSECT",VERTEX,{"disambiguationData":[OD(1.0)],"derivedFrom":[subQ1,subQ0]});Q31=makeQuery(id+"F8.imprint","IMPRINT",FACE,{"disambiguationData":[TD([[makeQuery(id+"F8.imprint","IMPRINT",EDGE,{"disambiguationData":[TD([[subQ2,-1.0]])],"derivedFrom":subQ1}),1.0]])]});}
            extrude(context, id + "F9", {"entities" : qUnion([Q0, Q1, Q2, Q3, Q4, Q5, Q6, Q7, Q8, Q9, Q10, Q11, Q12, Q13, Q14, Q15, Q16, Q17, Q18, Q19, Q20, Q21, Q22, Q23, Q24, Q25, Q26, Q27, Q28, Q29, Q30, Q31]), "depth" : 2 * mm, "offsetDistance" : 25 * mm});
        }
        {
            var Q0;
            {var subQ4=sQuery(id+"F8.wireOp",EDGE,"E45.3");Q0=makeQuery(id+"F8.imprint","IMPRINT",FACE,{"disambiguationData":[TD([[makeQuery(id+"F8.imprint","IMPRINT",EDGE,{"derivedFrom":subQ4}),1.0]])]});}
            var Q1;
            {var subQ5=sQuery(id+"F8.wireOp",EDGE,"E45.0");Q1=makeQuery(id+"F8.imprint","IMPRINT",FACE,{"disambiguationData":[TD([[makeQuery(id+"F8.imprint","IMPRINT",EDGE,{"derivedFrom":subQ5}),1.0]])]});}
            var Q2;
            {var subQ0=sQuery(id+"F8.wireOp",EDGE,"E38.0");var subQ1=sQuery(id+"F8.wireOp",EDGE,"E31");var subQ2=makeQuery(id+"F8.imprint","INTERSECT",VERTEX,{"disambiguationData":[OD(0.0)],"derivedFrom":[subQ1,subQ0]});Q2=makeQuery(id+"F8.imprint","IMPRINT",FACE,{"disambiguationData":[TD([[makeQuery(id+"F8.imprint","IMPRINT",EDGE,{"disambiguationData":[TD([[subQ2,-1.0]])],"derivedFrom":subQ1}),1.0]])]});}
            var Q3;
            {var subQ0=sQuery(id+"F8.wireOp",EDGE,"E39");var subQ1=sQuery(id+"F8.wireOp",EDGE,"E31");var subQ2=makeQuery(id+"F8.imprint","INTERSECT",VERTEX,{"disambiguationData":[OD(0.0)],"derivedFrom":[subQ1,subQ0]});Q3=makeQuery(id+"F8.imprint","IMPRINT",FACE,{"disambiguationData":[TD([[makeQuery(id+"F8.imprint","IMPRINT",EDGE,{"disambiguationData":[TD([[subQ2,1.0]])],"derivedFrom":subQ1}),1.0]])]});}
            var Q4;
            Q4=makeQuery(id+"F8.imprint","IMPRINT",FACE,{"disambiguationData":[TD([[makeQuery(id+"F8.imprint","IMPRINT",EDGE,{"derivedFrom":sQuery(id+"F8.wireOp",EDGE,"E44.0")}),1.0]])]});
            extrude(context, id + "F10", {"entities" : qUnion([Q0, Q1, Q2, Q3, Q4]), "operationType" : NewBodyOperationType.ADD, "oppositeDirection" : true, "depth" : 12 * mm, "offsetDistance" : 25 * mm});
        }
        {
            var Q0;
            Q0=makeQuery(id+"F10.opExtrude","CAP_FACE",FACE,{"disambiguationData":[OSD([sQuery(id+"F8.wireOp",EDGE,"E38.0"),sQuery(id+"F8.wireOp",EDGE,"E45.0"),sQuery(id+"F8.wireOp",EDGE,"E45.1"),sQuery(id+"F8.wireOp",EDGE,"E45.2"),sQuery(id+"F8.wireOp",EDGE,"E45.3"),sQuery(id+"F8.wireOp",EDGE,"E45.4"),sQuery(id+"F8.wireOp",EDGE,"E45.5")])],"isStart":false});
            var sketch = newSketch(context, id + "F11", { "sketchPlane" : qUnion([Q0])});
            skCircle(sketch, "E46", {"center": v(20.23, 8.65) * mm, "radius": 6 * mm});
            skCircle(sketch, "E47", {"center": v(20.23, 8.65) * mm, "radius": 2 * mm});
            skCircle(sketch, "E48", {"center": v(20.23, -8.65) * mm, "radius": 6 * mm});
            skCircle(sketch, "E49", {"center": v(20.23, -8.65) * mm, "radius": 2 * mm});
            skSolve(sketch);
        }
        {
            var Q0;
            Q0=makeQuery(id+"F11.imprint","IMPRINT",FACE,{"disambiguationData":[TD([[makeQuery(id+"F11.imprint","IMPRINT",EDGE,{"derivedFrom":sQuery(id+"F11.wireOp",EDGE,"E47")}),-1.0]])]});
            var Q1;
            Q1=makeQuery(id+"F11.imprint","IMPRINT",FACE,{"disambiguationData":[TD([[makeQuery(id+"F11.imprint","IMPRINT",EDGE,{"derivedFrom":sQuery(id+"F11.wireOp",EDGE,"E46")}),-1.0]])]});
            var Q2;
            Q2=makeQuery(id+"F11.imprint","IMPRINT",FACE,{"disambiguationData":[TD([[makeQuery(id+"F11.imprint","IMPRINT",EDGE,{"derivedFrom":sQuery(id+"F11.wireOp",EDGE,"E48")}),1.0]])]});
            extrude(context, id + "F12", {"entities" : qUnion([Q0, Q1, Q2]), "operationType" : NewBodyOperationType.ADD, "oppositeDirection" : true, "depth" : 2 * mm, "offsetDistance" : 25 * mm});
        }
        {
            var Q0;
            {var subQ0=sQuery(id+"F8.wireOp",EDGE,"E42");var subQ1=sQuery(id+"F8.wireOp",EDGE,"E29");var subQ2=makeQuery(id+"F8.imprint","INTERSECT",VERTEX,{"disambiguationData":[OD(0.0)],"derivedFrom":[subQ1,subQ0]});Q0=makeQuery(id+"F8.imprint","IMPRINT",FACE,{"disambiguationData":[TD([[makeQuery(id+"F8.imprint","IMPRINT",EDGE,{"disambiguationData":[TD([[subQ2,-1.0]])],"derivedFrom":subQ1}),-1.0]])]});}
            var Q1;
            {var subQ0=sQuery(id+"F8.wireOp",EDGE,"E42");var subQ1=sQuery(id+"F8.wireOp",EDGE,"E29");var subQ2=makeQuery(id+"F8.imprint","INTERSECT",VERTEX,{"disambiguationData":[OD(0.0)],"derivedFrom":[subQ1,subQ0]});Q1=makeQuery(id+"F8.imprint","IMPRINT",FACE,{"disambiguationData":[TD([[makeQuery(id+"F8.imprint","IMPRINT",EDGE,{"disambiguationData":[TD([[subQ2,-1.0]])],"derivedFrom":subQ1}),1.0]])]});}
            extrude(context, id + "F13", {"entities" : qUnion([Q0, Q1]), "operationType" : NewBodyOperationType.ADD, "oppositeDirection" : true, "depth" : 12 * mm, "offsetDistance" : 25 * mm});
        }
        {
            var Q0;
            Q0=makeQuery(id+"F9.opExtrude","SWEPT_EDGE",EDGE,{"disambiguationData":[OSD([sQuery(id+"F8.wireOp",EDGE,"E36"),sQuery(id+"F8.wireOp",EDGE,"E37")])]});
            var Q1;
            Q1=makeQuery(id+"F1.opExtrude","SWEPT_EDGE",EDGE,{"disambiguationData":[OSD([sQuery(id+"F0.wireOp",EDGE,"E11"),sQuery(id+"F0.wireOp",EDGE,"E12")])]});
            fillet(context, id + "F14", {"entities" : qUnion([Q0, Q1]), "radius" : 30 * mm, "tangentPropagation" : true, "allowEdgeOverflow" : false});
        }
        {
            var Q0;
            Q0=makeQuery(id+"F1.opExtrude","CAP_FACE",FACE,{"disambiguationData":[OSD([sQuery(id+"F0.wireOp",EDGE,"E4"),sQuery(id+"F0.wireOp",EDGE,"E5.0"),sQuery(id+"F0.wireOp",EDGE,"E6"),sQuery(id+"F0.wireOp",EDGE,"E9"),sQuery(id+"F0.wireOp",EDGE,"E10"),sQuery(id+"F0.wireOp",EDGE,"E11"),sQuery(id+"F0.wireOp",EDGE,"E12"),sQuery(id+"F0.wireOp",EDGE,"E13"),sQuery(id+"F0.wireOp",EDGE,"E14"),sQuery(id+"F0.wireOp",EDGE,"E15.0"),sQuery(id+"F0.wireOp",EDGE,"E17"),sQuery(id+"F0.wireOp",EDGE,"E18"),sQuery(id+"F0.wireOp",EDGE,"E19")])],"isStart":false});
            var sketch = newSketch(context, id + "F15", { "sketchPlane" : qUnion([Q0])});
            skCircle(sketch, "E50", {"center": v(69.08, 16.92) * mm, "radius": 2.85 * mm});
            skSolve(sketch);
        }
        {
            var Q0;
            Q0=makeQuery(id+"F15.imprint","IMPRINT",FACE,{"disambiguationData":[TD([[makeQuery(id+"F15.imprint","IMPRINT",EDGE,{"derivedFrom":sQuery(id+"F15.wireOp",EDGE,"E50")}),1.0]])]});
            extrude(context, id + "F16", {"entities" : qUnion([Q0]), "operationType" : NewBodyOperationType.REMOVE, "endBound" : BoundingType.UP_TO_NEXT, "oppositeDirection" : true, "depth" : 25 * mm, "offsetDistance" : 25 * mm});
        }
    });
